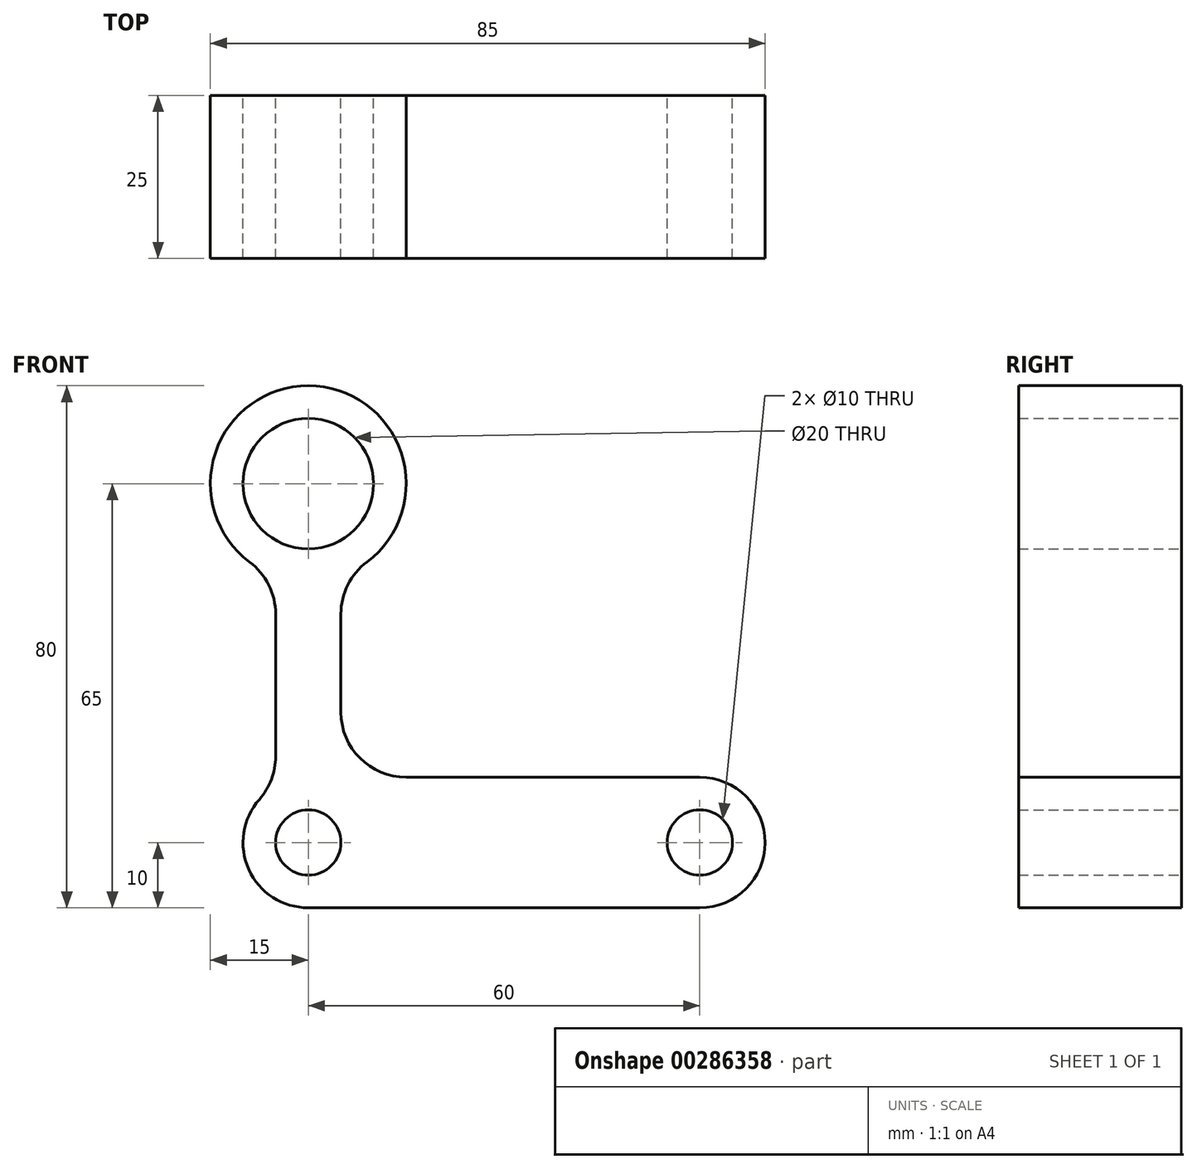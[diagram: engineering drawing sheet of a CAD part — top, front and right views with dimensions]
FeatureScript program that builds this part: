
annotation { "Feature Type Name" : "Feature", "Feature Type Description" : "" }
export const myFeature = defineFeature(function(context is Context, id is Id, definition is map)
    precondition{}
    {
        {
            var Q0;
            Q0=qCreatedBy(makeId("Front.planeOp"),FACE);
            var sketch = newSketch(context, id + "F0", { "sketchPlane" : qUnion([Q0])});
            skLineSegment(sketch, "E0", {"start": v(-101.63, 15) * mm, "end": v(-101.63, -40) * mm});
            skLineSegment(sketch, "E1", {"start": v(-101.63, 15) * mm, "end": v(-101.63, 30) * mm});
            skLineSegment(sketch, "E2", {"start": v(-101.63, 15) * mm, "end": v(-86.63, 15) * mm});
            skLineSegment(sketch, "E3", {"start": v(-101.63, 15) * mm, "end": v(-116.63, 15) * mm});
            skLineSegment(sketch, "E4", {"start": v(-86.63, 15) * mm, "end": v(-86.63, 15) * mm});
            skLineSegment(sketch, "E5", {"start": v(-86.63, 30) * mm, "end": v(-101.63, 30) * mm});
            skLineSegment(sketch, "E6", {"start": v(-101.63, 30) * mm, "end": v(-101.63, 30) * mm});
            skPoint(sketch, "E6.endSnap0", {"position": v(-94.13, 30) * mm});
            skLineSegment(sketch, "E7", {"start": v(-116.63, 15) * mm, "end": v(-116.63, 15) * mm});
            skLineSegment(sketch, "E8", {"start": v(-101.63, 0) * mm, "end": v(-101.63, 0) * mm});
            skPoint(sketch, "E9.visualSharp", {"position": v(-86.63, 30) * mm});
            skArc(sketch, "E9.filletArc", {"start": v(-86.63, 15) * mm, "mid": v(-91.02, 25.6) * mm, "end": v(-101.63, 30) * mm});
            skPoint(sketch, "E10.visualSharp", {"position": v(-116.63, 30) * mm});
            skArc(sketch, "E10.filletArc", {"start": v(-101.63, 30) * mm, "mid": v(-112.24, 25.6) * mm, "end": v(-116.63, 15) * mm});
            skPoint(sketch, "E11.visualSharp", {"position": v(-86.63, 0) * mm});
            skArc(sketch, "E11.filletArc", {"start": v(-92.63, 3) * mm, "mid": v(-88.21, 8.3) * mm, "end": v(-86.63, 15) * mm});
            skPoint(sketch, "E12.visualSharp", {"position": v(-116.63, 0) * mm});
            skArc(sketch, "E12.filletArc", {"start": v(-116.63, 15) * mm, "mid": v(-115.05, 8.3) * mm, "end": v(-110.63, 3) * mm});
            skLineSegment(sketch, "E13", {"start": v(-101.63, -6.43) * mm, "end": v(-96.63, -6.43) * mm});
            skLineSegment(sketch, "E14", {"start": v(-101.63, -6.43) * mm, "end": v(-106.63, -6.43) * mm});
            skLineSegment(sketch, "E15", {"start": v(-96.63, -6.43) * mm, "end": v(-96.63, -5) * mm});
            skCircle(sketch, "E16", {"center": v(-101.63, 15) * mm, "radius": 10 * mm});
            skArc(sketch, "E17.filletArc", {"start": v(-92.63, 3) * mm, "mid": v(-95.57, -0.53) * mm, "end": v(-96.63, -5) * mm});
            skArc(sketch, "E18.filletArc", {"start": v(-106.63, -5) * mm, "mid": v(-107.69, -0.53) * mm, "end": v(-110.63, 3) * mm});
            skLineSegment(sketch, "E19", {"start": v(-101.63, 30) * mm, "end": v(-101.63, -40) * mm});
            skCircle(sketch, "E20", {"center": v(-101.63, -40) * mm, "radius": 5 * mm});
            skLineSegment(sketch, "E21", {"start": v(-101.63, -40) * mm, "end": v(-111.63, -40) * mm});
            skLineSegment(sketch, "E22", {"start": v(-101.63, -40) * mm, "end": v(-101.63, -50) * mm});
            skLineSegment(sketch, "E23", {"start": v(-101.63, -50) * mm, "end": v(-101.63, -50) * mm});
            skLineSegment(sketch, "E24", {"start": v(-111.63, -40) * mm, "end": v(-111.63, -40) * mm});
            skLineSegment(sketch, "E25", {"start": v(-101.63, -30) * mm, "end": v(-101.63, -30) * mm});
            skLineSegment(sketch, "E26", {"start": v(-101.63, -50) * mm, "end": v(-91.63, -50) * mm});
            skLineSegment(sketch, "E27", {"start": v(-91.63, -50) * mm, "end": v(-91.63, -40) * mm});
            skLineSegment(sketch, "E28", {"start": v(-91.63, -40) * mm, "end": v(-91.63, -30) * mm});
            skLineSegment(sketch, "E29", {"start": v(-86.63, -30) * mm, "end": v(-91.63, -30) * mm});
            skLineSegment(sketch, "E30", {"start": v(-101.63, -30) * mm, "end": v(-96.63, -30) * mm});
            skLineSegment(sketch, "E31", {"start": v(-96.63, -20) * mm, "end": v(-96.63, -6.43) * mm});
            skPoint(sketch, "E32.visualSharp", {"position": v(-111.63, -30) * mm});
            skArc(sketch, "E32.filletArc", {"start": v(-109.13, -33.39) * mm, "mid": v(-110.98, -36.46) * mm, "end": v(-111.63, -40) * mm});
            skPoint(sketch, "E33.visualSharp", {"position": v(-111.63, -50) * mm});
            skArc(sketch, "E33.filletArc", {"start": v(-111.63, -40) * mm, "mid": v(-108.7, -47.07) * mm, "end": v(-101.63, -50) * mm});
            skLineSegment(sketch, "E34", {"start": v(-106.63, -6.43) * mm, "end": v(-106.63, -5) * mm});
            skLineSegment(sketch, "E35", {"start": v(-106.63, -6.43) * mm, "end": v(-106.63, -26.77) * mm});
            skArc(sketch, "E36.filletArc", {"start": v(-109.13, -33.39) * mm, "mid": v(-107.28, -30.3) * mm, "end": v(-106.63, -26.77) * mm});
            skPoint(sketch, "E37.newPointB", {"position": v(-101.63, -30) * mm});
            skArc(sketch, "E37.filletArc", {"start": v(-96.63, -20) * mm, "mid": v(-93.7, -27.07) * mm, "end": v(-86.63, -30) * mm});
            skLineSegment(sketch, "E38", {"start": v(-111.63, -40) * mm, "end": v(-41.63, -40) * mm});
            skCircle(sketch, "E39", {"center": v(-41.63, -40) * mm, "radius": 5 * mm});
            skLineSegment(sketch, "E40", {"start": v(-41.63, -40) * mm, "end": v(-41.63, -30) * mm});
            skLineSegment(sketch, "E41", {"start": v(-41.63, -30) * mm, "end": v(-41.63, -50) * mm});
            skLineSegment(sketch, "E42", {"start": v(-41.63, -50) * mm, "end": v(-41.63, -40) * mm});
            skLineSegment(sketch, "E43", {"start": v(-41.63, -40) * mm, "end": v(-31.63, -40) * mm});
            skLineSegment(sketch, "E44", {"start": v(-31.63, -40) * mm, "end": v(-31.63, -40) * mm});
            skLineSegment(sketch, "E45", {"start": v(-41.63, -30) * mm, "end": v(-41.63, -30) * mm});
            skLineSegment(sketch, "E46", {"start": v(-41.63, -50) * mm, "end": v(-41.63, -50) * mm});
            skPoint(sketch, "E47.visualSharp", {"position": v(-31.63, -30) * mm});
            skArc(sketch, "E47.filletArc", {"start": v(-31.63, -40) * mm, "mid": v(-34.56, -32.93) * mm, "end": v(-41.63, -30) * mm});
            skPoint(sketch, "E48.visualSharp", {"position": v(-31.63, -50) * mm});
            skArc(sketch, "E48.filletArc", {"start": v(-41.63, -50) * mm, "mid": v(-34.56, -47.07) * mm, "end": v(-31.63, -40) * mm});
            skLineSegment(sketch, "E49", {"start": v(-41.63, -50) * mm, "end": v(-91.63, -50) * mm});
            skLineSegment(sketch, "E50", {"start": v(-41.63, -30) * mm, "end": v(-86.63, -30) * mm});
            skSolve(sketch);
        }
        {
            var Q0;
            {var subQ4=sQuery(id+"F0.wireOp",EDGE,"E12.filletArc");Q0=makeQuery(id+"F0.imprint","IMPRINT",FACE,{"disambiguationData":[TD([[makeQuery(id+"F0.imprint","IMPRINT",EDGE,{"derivedFrom":subQ4}),1.0]])]});}
            var Q1;
            {var subQ1=sQuery(id+"F0.wireOp",EDGE,"E11.filletArc");Q1=makeQuery(id+"F0.imprint","IMPRINT",FACE,{"disambiguationData":[TD([[makeQuery(id+"F0.imprint","IMPRINT",EDGE,{"derivedFrom":subQ1}),1.0]])]});}
            var Q2;
            {var subQ0=sQuery(id+"F0.wireOp",EDGE,"E9.filletArc");Q2=makeQuery(id+"F0.imprint","IMPRINT",FACE,{"disambiguationData":[TD([[makeQuery(id+"F0.imprint","IMPRINT",EDGE,{"derivedFrom":subQ0}),1.0]])]});}
            var Q3;
            {var subQ0=sQuery(id+"F0.wireOp",EDGE,"E10.filletArc");Q3=makeQuery(id+"F0.imprint","IMPRINT",FACE,{"disambiguationData":[TD([[makeQuery(id+"F0.imprint","IMPRINT",EDGE,{"derivedFrom":subQ0}),1.0]])]});}
            var Q4;
            {var subQ7=sQuery(id+"F0.wireOp",EDGE,"E13");Q4=makeQuery(id+"F0.imprint","IMPRINT",FACE,{"disambiguationData":[TD([[makeQuery(id+"F0.imprint","IMPRINT",EDGE,{"derivedFrom":subQ7}),-1.0]])]});}
            var Q5;
            {var subQ6=sQuery(id+"F0.wireOp",EDGE,"E14");Q5=makeQuery(id+"F0.imprint","IMPRINT",FACE,{"disambiguationData":[TD([[makeQuery(id+"F0.imprint","IMPRINT",EDGE,{"derivedFrom":subQ6}),1.0]])]});}
            var Q6;
            {var subQ5=sQuery(id+"F0.wireOp",EDGE,"E33.filletArc");Q6=makeQuery(id+"F0.imprint","IMPRINT",FACE,{"disambiguationData":[TD([[makeQuery(id+"F0.imprint","IMPRINT",EDGE,{"derivedFrom":subQ5}),1.0]])]});}
            var Q7;
            {var subQ1=sQuery(id+"F0.wireOp",EDGE,"E26");Q7=makeQuery(id+"F0.imprint","IMPRINT",FACE,{"disambiguationData":[TD([[makeQuery(id+"F0.imprint","IMPRINT",EDGE,{"derivedFrom":subQ1}),1.0]])]});}
            var Q8;
            {var subQ4=sQuery(id+"F0.wireOp",EDGE,"E27");Q8=makeQuery(id+"F0.imprint","IMPRINT",FACE,{"disambiguationData":[TD([[makeQuery(id+"F0.imprint","IMPRINT",EDGE,{"derivedFrom":subQ4}),-1.0]])]});}
            var Q9;
            {var subQ1=sQuery(id+"F0.wireOp",EDGE,"E28");Q9=makeQuery(id+"F0.imprint","IMPRINT",FACE,{"disambiguationData":[TD([[makeQuery(id+"F0.imprint","IMPRINT",EDGE,{"derivedFrom":subQ1}),-1.0]])]});}
            var Q10;
            {var subQ5=sQuery(id+"F0.wireOp",EDGE,"E48.filletArc");Q10=makeQuery(id+"F0.imprint","IMPRINT",FACE,{"disambiguationData":[TD([[makeQuery(id+"F0.imprint","IMPRINT",EDGE,{"derivedFrom":subQ5}),1.0]])]});}
            var Q11;
            {var subQ5=sQuery(id+"F0.wireOp",EDGE,"E47.filletArc");Q11=makeQuery(id+"F0.imprint","IMPRINT",FACE,{"disambiguationData":[TD([[makeQuery(id+"F0.imprint","IMPRINT",EDGE,{"derivedFrom":subQ5}),1.0]])]});}
            extrude(context, id + "F1", {"entities" : qUnion([Q0, Q1, Q2, Q3, Q4, Q5, Q6, Q7, Q8, Q9, Q10, Q11]), "depth" : 25 * mm});
        }
    });
